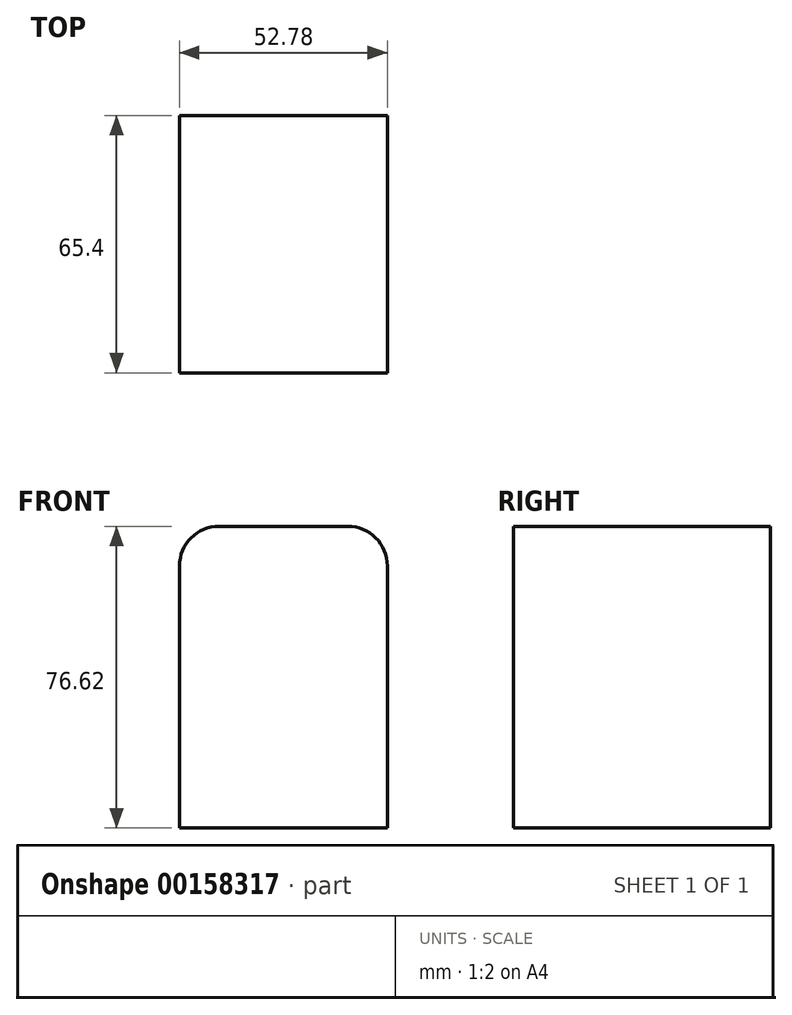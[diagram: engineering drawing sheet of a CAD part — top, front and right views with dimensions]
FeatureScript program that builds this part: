
annotation { "Feature Type Name" : "Feature", "Feature Type Description" : "" }
export const myFeature = defineFeature(function(context is Context, id is Id, definition is map)
    precondition{}
    {
        {
            var Q0;
            Q0=qCreatedBy(makeId("Front.planeOp"),FACE);
            var sketch = newSketch(context, id + "F1", { "sketchPlane" : qUnion([Q0])});
            skLineSegment(sketch, "E0.bottom", {"start": v(52.78, 76.62) * mm, "end": v(0, 76.62) * mm});
            skLineSegment(sketch, "E0.top", {"start": v(52.78, 0) * mm, "end": v(0, 0) * mm});
            skLineSegment(sketch, "E0.left", {"start": v(52.78, 76.62) * mm, "end": v(52.78, 0) * mm});
            skLineSegment(sketch, "E0.right", {"start": v(0, 76.62) * mm, "end": v(0, 0) * mm});
            skSolve(sketch);
        }
        {
            var Q0;
            Q0=makeQuery(id+"F1.imprint","IMPRINT",FACE,{"disambiguationData":[TD([[makeQuery(id+"F1.imprint","IMPRINT",EDGE,{"derivedFrom":sQuery(id+"F1.wireOp",EDGE,"E0.bottom")}),1.0]])]});
            extrude(context, id + "F2", {"entities" : qUnion([Q0]), "depth" : 65.4 * mm});
        }
        {
            var Q0;
            Q0=makeQuery(id+"F2.opExtrude","SWEPT_EDGE",EDGE,{"disambiguationData":[OSD([sQuery(id+"F1.wireOp",EDGE,"E0.bottom"),sQuery(id+"F1.wireOp",EDGE,"E0.left")])]});
            var Q1;
            Q1=makeQuery(id+"F2.opExtrude","SWEPT_EDGE",EDGE,{"disambiguationData":[OSD([sQuery(id+"F1.wireOp",EDGE,"E0.bottom"),sQuery(id+"F1.wireOp",EDGE,"E0.right")])]});
            fillet(context, id + "F0", {"entities" : qUnion([Q0, Q1]), "radius" : 10 * mm, "tangentPropagation" : true, "allowEdgeOverflow" : false});
        }
    });
